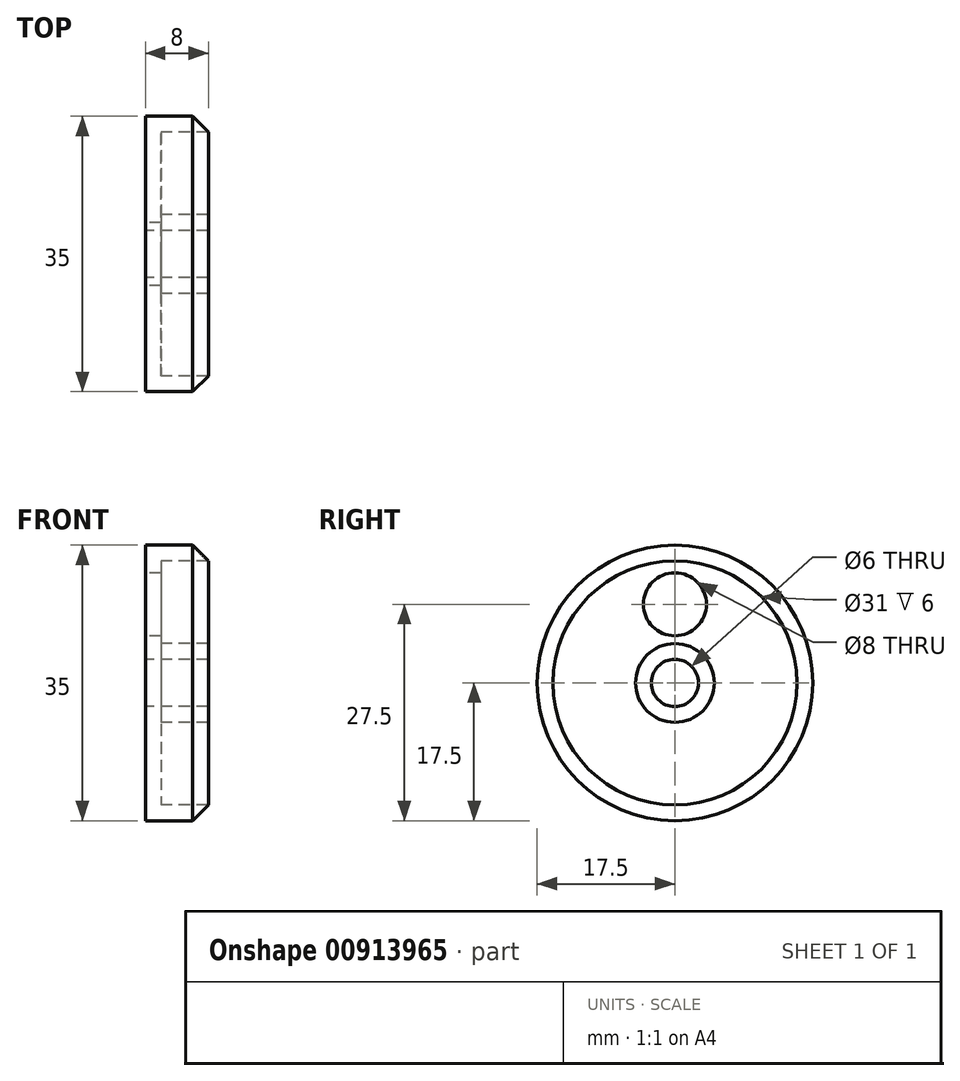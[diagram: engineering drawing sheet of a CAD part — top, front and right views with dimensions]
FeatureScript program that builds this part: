
annotation { "Feature Type Name" : "Feature", "Feature Type Description" : "" }
export const myFeature = defineFeature(function(context is Context, id is Id, definition is map)
    precondition{}
    {
        {
            var Q0;
            Q0=qCreatedBy(makeId("Top.planeOp"),FACE);
            var sketch = newSketch(context, id + "F0", { "sketchPlane" : qUnion([Q0])});
            skLineSegment(sketch, "E0.bottom", {"start": v(0, 0) * mm, "end": v(8, 0) * mm});
            skLineSegment(sketch, "E0.top", {"start": v(0, 17.5) * mm, "end": v(8, 17.5) * mm});
            skLineSegment(sketch, "E0.left", {"start": v(0, 0) * mm, "end": v(0, 17.5) * mm});
            skLineSegment(sketch, "E0.right", {"start": v(8, 0) * mm, "end": v(8, 17.5) * mm});
            skSolve(sketch);
        }
        {
            var Q0;
            Q0=makeQuery(id+"F0.imprint","IMPRINT",FACE,{"disambiguationData":[TD([[makeQuery(id+"F0.imprint","IMPRINT",EDGE,{"derivedFrom":sQuery(id+"F0.wireOp",EDGE,"E0.bottom")}),1.0]])]});
            var Q1;
            Q1=sQuery(id+"F0.wireOp",EDGE,"E0.bottom");
            revolve(context, id + "F1", {"surfaceOperationType" : NewSurfaceOperationType.NEW, "entities" : qUnion([Q0]), "axis" : qUnion([Q1]), "revolveType" : RevolveType.FULL});
        }
        {
            var Q0;
            Q0=qCreatedBy(makeId("Right.planeOp"),FACE);
            var sketch = newSketch(context, id + "F2", { "sketchPlane" : qUnion([Q0])});
            skPoint(sketch, "E1", {"position": v(0, 0) * mm});
            skSolve(sketch);
        }
        {
            var Q0;
            Q0=sQuery(id+"F2.wireOp",VERTEX,"E1");
            var Q1;
            Q1=makeQuery(id+"F1.opRevolve","SWEPT_BODY",BODY,{"disambiguationData":[OSD([sQuery(id+"F0.wireOp",EDGE,"E0.bottom"),sQuery(id+"F0.wireOp",EDGE,"E0.top"),sQuery(id+"F0.wireOp",EDGE,"E0.left"),sQuery(id+"F0.wireOp",EDGE,"E0.right")])]});
            hole(context, id + "F3", {"style" : HoleStyle.SIMPLE, "endStyle" : HoleEndStyle.BLIND, "oppositeDirection" : true, "holeDiameter" : 6 * mm, "majorDiameter" : 5 * mm, "holeDepth" : 12 * mm, "isTappedThrough" : true, "tappedDepth" : 12 * mm, "tapClearance" : 3, "locations" : qUnion([Q0]), "scope" : qUnion([Q1])});
        }
        {
            var Q0;
            Q0=makeQuery(id+"F1.opRevolve","SWEPT_FACE",FACE,{"disambiguationData":[OSD([sQuery(id+"F0.wireOp",EDGE,"E0.right")])]});
            shell(context, id + "F4", {"entities" : qUnion([Q0]), "thickness" : 2 * mm});
        }
        {
            var Q0;
            Q0=qCreatedBy(makeId("Right.planeOp"),FACE);
            var sketch = newSketch(context, id + "F5", { "sketchPlane" : qUnion([Q0])});
            skPoint(sketch, "E2", {"position": v(0, 10) * mm});
            skSolve(sketch);
        }
        {
            var Q0;
            Q0=sQuery(id+"F5.wireOp",VERTEX,"E2");
            var Q1;
            Q1=makeQuery(id+"F1.opRevolve","SWEPT_BODY",BODY,{"disambiguationData":[OSD([sQuery(id+"F0.wireOp",EDGE,"E0.bottom"),sQuery(id+"F0.wireOp",EDGE,"E0.top"),sQuery(id+"F0.wireOp",EDGE,"E0.left"),sQuery(id+"F0.wireOp",EDGE,"E0.right")])]});
            hole(context, id + "F6", {"style" : HoleStyle.SIMPLE, "endStyle" : HoleEndStyle.BLIND, "oppositeDirection" : true, "holeDiameter" : 8 * mm, "majorDiameter" : 5 * mm, "holeDepth" : 12 * mm, "isTappedThrough" : true, "tappedDepth" : 12 * mm, "tapClearance" : 3, "locations" : qUnion([Q0]), "scope" : qUnion([Q1])});
        }
        {
            var Q0;
            Q0=makeQuery(id+"F1.opRevolve","SWEPT_EDGE",EDGE,{"disambiguationData":[OSD([sQuery(id+"F0.wireOp",EDGE,"E0.top"),sQuery(id+"F0.wireOp",EDGE,"E0.right")])]});
            chamfer(context, id + "F7", {"entities" : qUnion([Q0]), "width" : 2 * mm, "tangentPropagation" : true});
        }
    });
